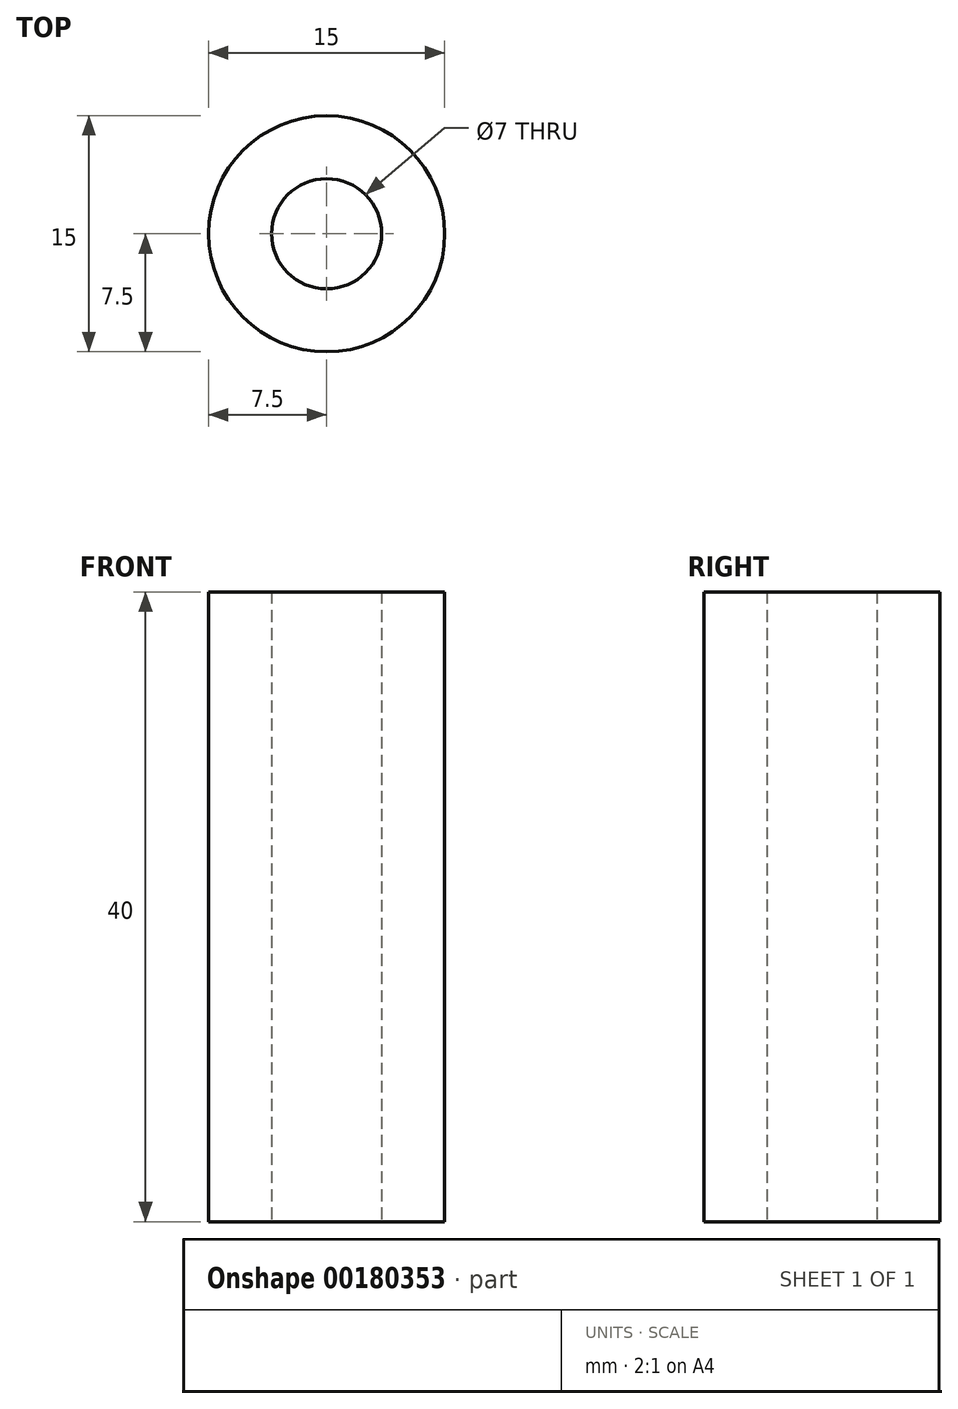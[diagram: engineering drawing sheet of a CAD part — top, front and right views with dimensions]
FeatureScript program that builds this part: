
annotation { "Feature Type Name" : "Feature", "Feature Type Description" : "" }
export const myFeature = defineFeature(function(context is Context, id is Id, definition is map)
    precondition{}
    {
        {
            var Q0;
            Q0=qCreatedBy(makeId("Top.planeOp"),FACE);
            var sketch = newSketch(context, id + "F0", { "sketchPlane" : qUnion([Q0])});
            skCircle(sketch, "E0", {"center": v(0, 0) * mm, "radius": 7.5 * mm});
            skCircle(sketch, "E1", {"center": v(0, 0) * mm, "radius": 3.5 * mm});
            skSolve(sketch);
        }
        {
            var Q0;
            Q0 = qSketchRegion(id + "F0", true);
            extrude(context, id + "F1", {"entities" : qUnion([Q0]), "depth" : 40 * mm});
        }
    });
